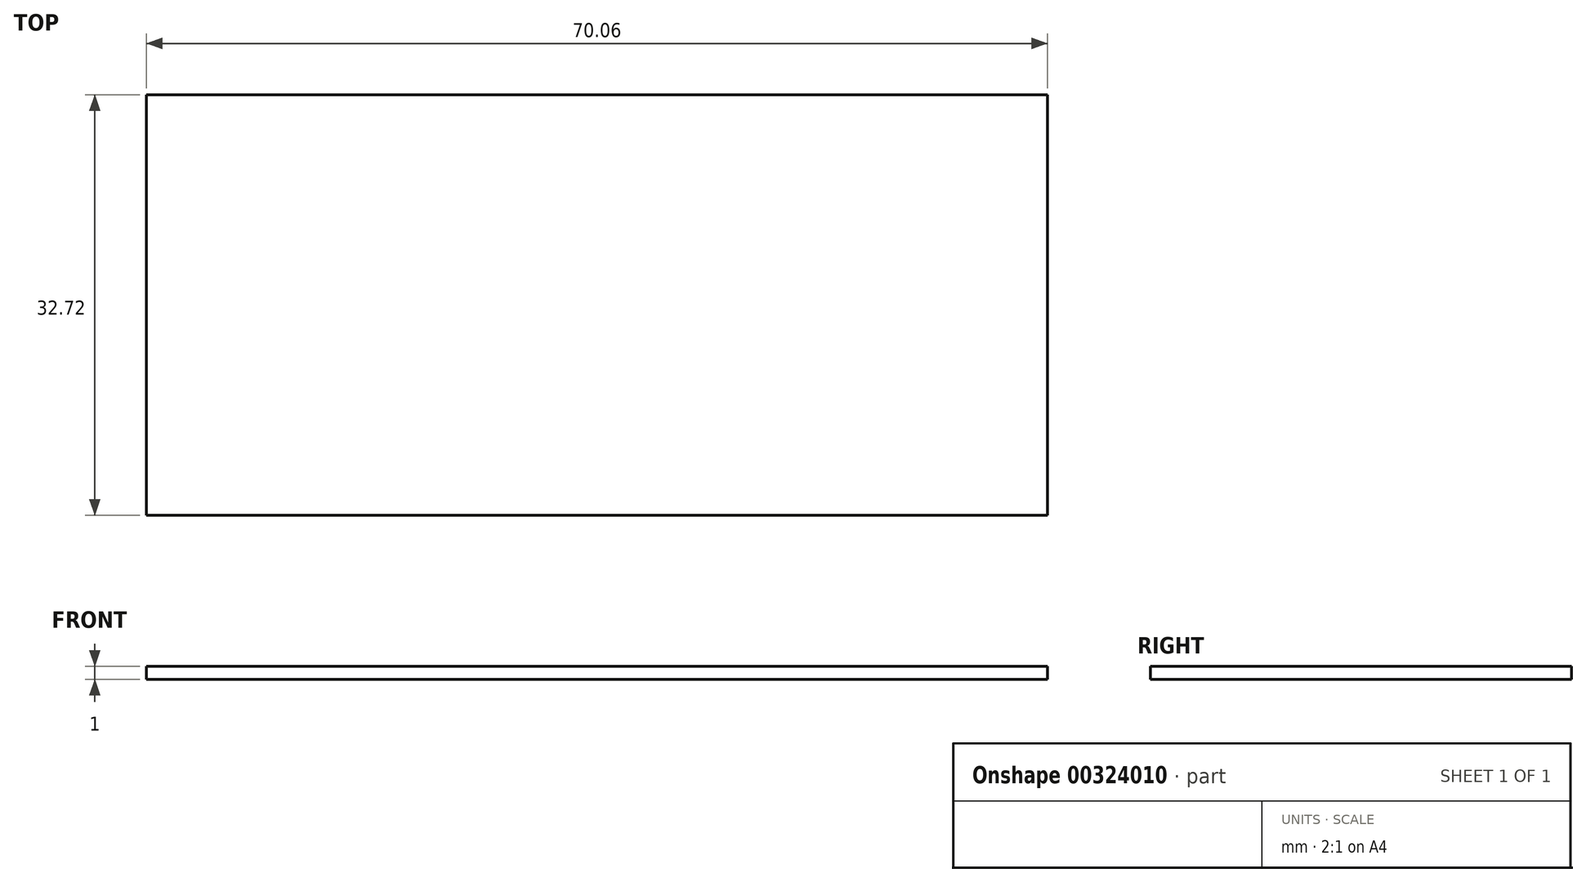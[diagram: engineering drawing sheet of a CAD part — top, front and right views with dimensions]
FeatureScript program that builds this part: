
annotation { "Feature Type Name" : "Feature", "Feature Type Description" : "" }
export const myFeature = defineFeature(function(context is Context, id is Id, definition is map)
    precondition{}
    {
        {
            var Q0;
            Q0=qCreatedBy(makeId("Top.planeOp"),FACE);
            var sketch = newSketch(context, id + "F0", { "sketchPlane" : qUnion([Q0])});
            skLineSegment(sketch, "E0.bottom", {"start": v(-35.03, 16.36) * mm, "end": v(35.03, 16.36) * mm});
            skLineSegment(sketch, "E0.top", {"start": v(-35.03, -16.36) * mm, "end": v(35.03, -16.36) * mm});
            skLineSegment(sketch, "E0.left", {"start": v(-35.03, 16.36) * mm, "end": v(-35.03, -16.36) * mm});
            skLineSegment(sketch, "E0.right", {"start": v(35.03, 16.36) * mm, "end": v(35.03, -16.36) * mm});
            skPoint(sketch, "E1", {"position": v(-31.03, 12.36) * mm});
            skPoint(sketch, "E2", {"position": v(-31.03, -10.97) * mm});
            skPoint(sketch, "E3", {"position": v(30.25, -10.97) * mm});
            skPoint(sketch, "E4", {"position": v(30.25, 12.36) * mm});
            skPoint(sketch, "E5", {"position": v(-35.03, 0) * mm});
            skPoint(sketch, "E6", {"position": v(0, 16.36) * mm});
            skSolve(sketch);
        }
        {
            var Q0;
            Q0=makeQuery(id+"F0.imprint","IMPRINT",FACE,{"disambiguationData":[TD([[makeQuery(id+"F0.imprint","IMPRINT",EDGE,{"derivedFrom":sQuery(id+"F0.wireOp",EDGE,"E0.bottom")}),-1.0]])]});
            extrude(context, id + "F1", {"entities" : qUnion([Q0]), "depth" : 1 * mm});
        }
    });
